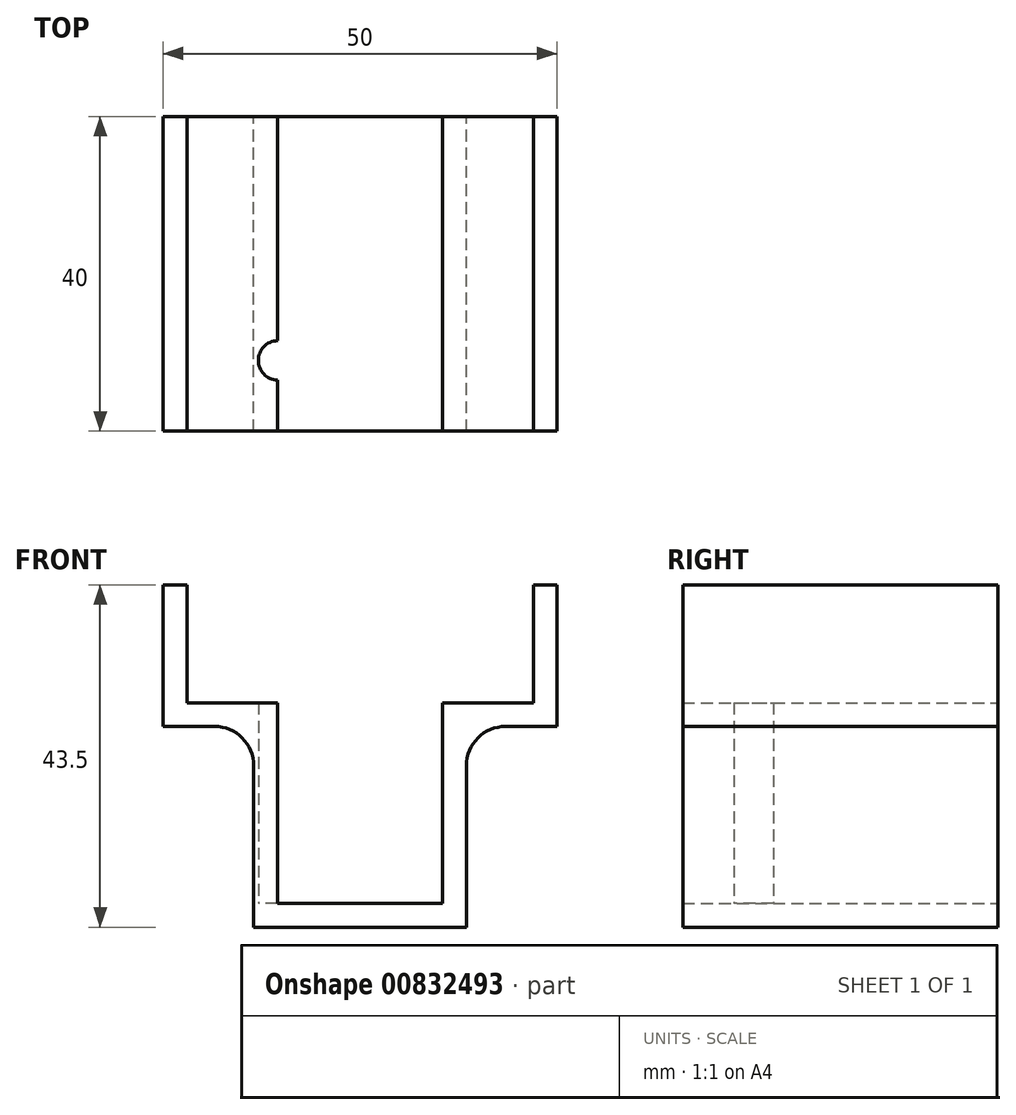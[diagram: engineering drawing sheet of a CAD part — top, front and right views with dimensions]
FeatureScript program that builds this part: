
annotation { "Feature Type Name" : "Feature", "Feature Type Description" : "" }
export const myFeature = defineFeature(function(context is Context, id is Id, definition is map)
    precondition{}
    {
        {
            var Q0;
            Q0=qCreatedBy(makeId("Front.planeOp"),FACE);
            var sketch = newSketch(context, id + "F0", { "sketchPlane" : qUnion([Q0])});
            skLineSegment(sketch, "E0", {"start": v(0, 0) * mm, "end": v(10.5, 0) * mm});
            skLineSegment(sketch, "E1", {"start": v(10.5, 0) * mm, "end": v(10.5, 25.5) * mm});
            skLineSegment(sketch, "E2", {"start": v(10.5, 25.5) * mm, "end": v(22, 25.5) * mm});
            skLineSegment(sketch, "E3", {"start": v(22, 25.5) * mm, "end": v(22, 40.5) * mm});
            skLineSegment(sketch, "E4.0", {"start": v(25, 22.5) * mm, "end": v(25, 40.5) * mm});
            skLineSegment(sketch, "E4.1", {"start": v(13.5, 22.5) * mm, "end": v(25, 22.5) * mm});
            skLineSegment(sketch, "E4.2", {"start": v(13.5, -3) * mm, "end": v(13.5, 22.5) * mm});
            skLineSegment(sketch, "E4.3", {"start": v(0, -3) * mm, "end": v(13.5, -3) * mm});
            skLineSegment(sketch, "E5", {"start": v(0, -4.58) * mm, "end": v(0, 37.69) * mm, "construction": true});
            skLineSegment(sketch, "E6", {"start": v(25, 40.5) * mm, "end": v(22, 40.5) * mm, "construction": true});
            skLineSegment(sketch, "E7.MirrorCS", {"start": v(0, 0) * mm, "end": v(-10.5, 0) * mm});
            skLineSegment(sketch, "E8.MirrorCS", {"start": v(-10.5, 0) * mm, "end": v(-10.5, 25.5) * mm});
            skLineSegment(sketch, "E9.MirrorCS", {"start": v(-10.5, 25.5) * mm, "end": v(-22, 25.5) * mm});
            skLineSegment(sketch, "E10.MirrorCS", {"start": v(-22, 25.5) * mm, "end": v(-22, 40.5) * mm});
            skLineSegment(sketch, "E11.MirrorCS", {"start": v(-25, 40.5) * mm, "end": v(-22, 40.5) * mm, "construction": true});
            skLineSegment(sketch, "E12.MirrorCS", {"start": v(-25, 22.5) * mm, "end": v(-25, 40.5) * mm});
            skLineSegment(sketch, "E13.MirrorCS", {"start": v(-13.5, 22.5) * mm, "end": v(-25, 22.5) * mm});
            skLineSegment(sketch, "E14.MirrorCS", {"start": v(-13.5, -3) * mm, "end": v(-13.5, 22.5) * mm});
            skLineSegment(sketch, "E15.MirrorCS", {"start": v(0, -3) * mm, "end": v(-13.5, -3) * mm});
            skLineSegment(sketch, "E16", {"start": v(-22, 40.5) * mm, "end": v(-25, 40.5) * mm});
            skLineSegment(sketch, "E17", {"start": v(25, 40.5) * mm, "end": v(22, 40.5) * mm});
            skSolve(sketch);
        }
        {
            var Q0;
            Q0=makeQuery(id+"F0.imprint","IMPRINT",FACE,{"disambiguationData":[TD([[makeQuery(id+"F0.imprint","IMPRINT",EDGE,{"derivedFrom":sQuery(id+"F0.wireOp",EDGE,"E0")}),-1.0]])]});
            extrude(context, id + "F1", {"entities" : qUnion([Q0]), "depth" : 40 * mm, "offsetDistance" : 25 * mm});
        }
        {
            var Q0;
            Q0=makeQuery(id+"F1.opExtrude","SWEPT_EDGE",EDGE,{"disambiguationData":[OSD([sQuery(id+"F0.wireOp",EDGE,"E13.MirrorCS"),sQuery(id+"F0.wireOp",EDGE,"E14.MirrorCS")])]});
            var Q1;
            Q1=makeQuery(id+"F1.opExtrude","SWEPT_EDGE",EDGE,{"disambiguationData":[OSD([sQuery(id+"F0.wireOp",EDGE,"E4.1"),sQuery(id+"F0.wireOp",EDGE,"E4.2")])]});
            fillet(context, id + "F2", {"entities" : qUnion([Q0, Q1]), "radius" : 5 * mm, "tangentPropagation" : true, "allowEdgeOverflow" : false});
        }
        {
            var Q0;
            Q0=qCreatedBy(makeId("Top.planeOp"),FACE);
            var sketch = newSketch(context, id + "F3", { "sketchPlane" : qUnion([Q0])});
            skPoint(sketch, "E18", {"position": v(-10.42, -31) * mm});
            skCircle(sketch, "E19", {"center": v(-10.42, -31) * mm, "radius": 2.5 * mm});
            skCircle(sketch, "E20.MirrorC", {"center": v(10.42, -31) * mm, "radius": 2.5 * mm});
            skSolve(sketch);
        }
        {
            var Q0;
            Q0=makeQuery(id+"F3.imprint","IMPRINT",FACE,{"disambiguationData":[TD([[makeQuery(id+"F3.imprint","IMPRINT",EDGE,{"derivedFrom":sQuery(id+"F3.wireOp",EDGE,"E19")}),1.0]])]});
            var Q1;
            Q1=makeQuery(id+"F3.imprint","IMPRINT",FACE,{"disambiguationData":[TD([[makeQuery(id+"F3.imprint","IMPRINT",EDGE,{"derivedFrom":sQuery(id+"F3.wireOp",EDGE,"E20.MirrorC")}),-1.0]])]});
            extrude(context, id + "F4", {"entities" : qUnion([Q0, Q1]), "operationType" : NewBodyOperationType.REMOVE, "depth" : 27 * mm, "offsetDistance" : 25 * mm});
        }
    });
